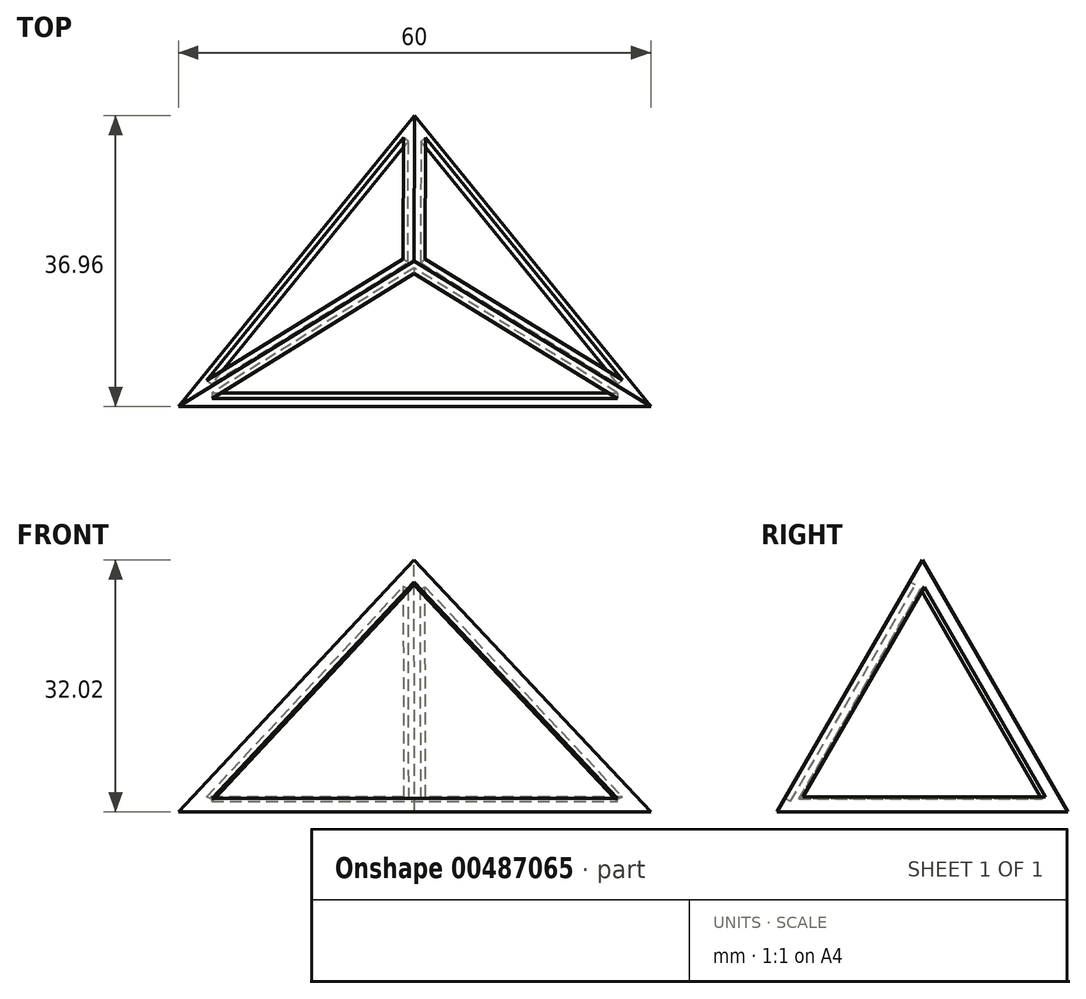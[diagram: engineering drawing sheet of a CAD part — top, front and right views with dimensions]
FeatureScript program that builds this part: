
annotation { "Feature Type Name" : "Feature", "Feature Type Description" : "" }
export const myFeature = defineFeature(function(context is Context, id is Id, definition is map)
    precondition{}
    {
        {
            var Q0;
            Q0=qCreatedBy(makeId("Top.planeOp"),FACE);
            var sketch = newSketch(context, id + "F0", { "sketchPlane" : qUnion([Q0])});
            skLineSegment(sketch, "E0.bottom", {"start": v(30, -36.96) * mm, "end": v(-30, -36.96) * mm});
            skPoint(sketch, "E0.middle", {"position": v(0, 0) * mm});
            skLineSegment(sketch, "E1", {"start": v(30, -36.96) * mm, "end": v(0, 0) * mm});
            skLineSegment(sketch, "E2", {"start": v(-30, -36.96) * mm, "end": v(0, 0) * mm});
            skSolve(sketch);
        }
        {
            var Q0;
            Q0=sQuery(id+"F0.wireOp",EDGE,"E0.bottom");
            cPlane(context, id + "F1", {"entities" : qUnion([Q0]), "cplaneType" : CPlaneType.LINE_ANGLE, "offset" : 25.4 * mm, "angle" : 30 * degree, "width" : 152.4 * mm, "height" : 152.4 * mm});
        }
        {
            var Q0;
            Q0=qCreatedBy(id+"F1.planeOp",FACE);
            var sketch = newSketch(context, id + "F2", { "sketchPlane" : qUnion([Q0])});
            skLineSegment(sketch, "E3.bottom", {"start": v(29.92, -18.46) * mm, "end": v(-30.08, -18.46) * mm});
            skLineSegment(sketch, "E4", {"start": v(29.92, -18.46) * mm, "end": v(-0.08, 18.5) * mm});
            skLineSegment(sketch, "E5", {"start": v(-30.08, -18.46) * mm, "end": v(-0.08, 18.5) * mm});
            skSolve(sketch);
        }
        {
            var Q0;
            Q0=makeQuery(id+"F0.imprint","IMPRINT",FACE,{"disambiguationData":[TD([[makeQuery(id+"F0.imprint","IMPRINT",EDGE,{"derivedFrom":sQuery(id+"F0.wireOp",EDGE,"E0.bottom")}),-1.0]])]});
            var Q1;
            Q1=sQuery(id+"F2.wireOp",VERTEX,"E5.end");
            loft(context, id + "F3", {"sheetProfilesArray" : [{ "sheetProfileEntities" : qUnion([Q0]) }, { "sheetProfileEntities" : qUnion([Q1]) }]});
        }
        {
            var Q0;
            {var subQ0=sQuery(id+"F0.wireOp",EDGE,"E2");var subQ1=sQuery(id+"F0.wireOp",EDGE,"E1");var subQ2=sQuery(id+"F0.wireOp",EDGE,"E0.bottom");Q0=makeQuery(id+"F3.opLoft","SWEPT_FACE",FACE,{"disambiguationData":[OSD([subQ2,subQ1,subQ0]),TDD([makeQuery(id+"F0.imprint","INTERSECT",VERTEX,{"derivedFrom":[subQ2,subQ0]}),makeQuery(id+"F0.imprint","INTERSECT",VERTEX,{"derivedFrom":[subQ1,subQ0]}),makeQuery(id+"F0.imprint","IMPRINT",EDGE,{"derivedFrom":subQ0})])]});}
            var sketch = newSketch(context, id + "F4", { "sketchPlane" : qUnion([Q0])});
            skLineSegment(sketch, "E6.0", {"start": v(41.78, -9.43) * mm, "end": v(22.63, 25.33) * mm});
            skLineSegment(sketch, "E6.1", {"start": v(3.5, 1.14) * mm, "end": v(41.78, -9.43) * mm});
            skLineSegment(sketch, "E6.2", {"start": v(22.63, 25.33) * mm, "end": v(3.5, 1.14) * mm});
            skSolve(sketch);
        }
        {
            var Q0;
            {var subQ0=sQuery(id+"F0.wireOp",EDGE,"E0.bottom");var subQ1=sQuery(id+"F0.wireOp",EDGE,"E2");var subQ2=sQuery(id+"F0.wireOp",EDGE,"E1");Q0=makeQuery(id+"F3.opLoft","SWEPT_FACE",FACE,{"disambiguationData":[OSD([subQ0,subQ2,subQ1]),TDD([makeQuery(id+"F0.imprint","INTERSECT",VERTEX,{"derivedFrom":[subQ0,subQ2]}),makeQuery(id+"F0.imprint","INTERSECT",VERTEX,{"derivedFrom":[subQ0,subQ1]}),makeQuery(id+"F0.imprint","IMPRINT",EDGE,{"derivedFrom":subQ0})])]});}
            var sketch = newSketch(context, id + "F5", { "sketchPlane" : qUnion([Q0])});
            skLineSegment(sketch, "E7.0", {"start": v(25.75, -16.46) * mm, "end": v(-0.07, 15.28) * mm});
            skLineSegment(sketch, "E7.1", {"start": v(-25.76, -16.46) * mm, "end": v(25.75, -16.46) * mm});
            skLineSegment(sketch, "E7.2", {"start": v(-0.07, 15.28) * mm, "end": v(-25.76, -16.46) * mm});
            skSolve(sketch);
        }
        {
            var Q0;
            {var subQ0=sQuery(id+"F0.wireOp",EDGE,"E1");var subQ1=sQuery(id+"F0.wireOp",EDGE,"E2");var subQ2=sQuery(id+"F0.wireOp",EDGE,"E0.bottom");Q0=makeQuery(id+"F3.opLoft","SWEPT_FACE",FACE,{"disambiguationData":[OSD([subQ2,subQ0,subQ1]),TDD([makeQuery(id+"F0.imprint","INTERSECT",VERTEX,{"derivedFrom":[subQ2,subQ0]}),makeQuery(id+"F0.imprint","INTERSECT",VERTEX,{"derivedFrom":[subQ0,subQ1]}),makeQuery(id+"F0.imprint","IMPRINT",EDGE,{"derivedFrom":subQ0})])]});}
            var sketch = newSketch(context, id + "F6", { "sketchPlane" : qUnion([Q0])});
            skLineSegment(sketch, "E8.0", {"start": v(-3.51, 1.14) * mm, "end": v(-22.6, 25.31) * mm});
            skLineSegment(sketch, "E8.1", {"start": v(-41.72, -9.5) * mm, "end": v(-3.51, 1.14) * mm});
            skLineSegment(sketch, "E8.2", {"start": v(-22.6, 25.31) * mm, "end": v(-41.72, -9.5) * mm});
            skSolve(sketch);
        }
        {
            var Q0;
            Q0=makeQuery(id+"F5.imprint","IMPRINT",FACE,{"disambiguationData":[TD([[makeQuery(id+"F5.imprint","IMPRINT",EDGE,{"derivedFrom":sQuery(id+"F5.wireOp",EDGE,"E7.0")}),1.0]])]});
            extrude(context, id + "F7", {"entities" : qUnion([Q0]), "operationType" : NewBodyOperationType.REMOVE, "oppositeDirection" : true, "depth" : 0.81 * mm});
        }
        {
            var Q0;
            Q0=makeQuery(id+"F6.imprint","IMPRINT",FACE,{"disambiguationData":[TD([[makeQuery(id+"F6.imprint","IMPRINT",EDGE,{"derivedFrom":sQuery(id+"F6.wireOp",EDGE,"E8.0")}),1.0]])]});
            extrude(context, id + "F8", {"entities" : qUnion([Q0]), "operationType" : NewBodyOperationType.REMOVE, "oppositeDirection" : true, "depth" : 0.81 * mm});
        }
        {
            var Q0;
            Q0=makeQuery(id+"F4.imprint","IMPRINT",FACE,{"disambiguationData":[TD([[makeQuery(id+"F4.imprint","IMPRINT",EDGE,{"derivedFrom":sQuery(id+"F4.wireOp",EDGE,"E6.0")}),1.0]])]});
            extrude(context, id + "F9", {"entities" : qUnion([Q0]), "operationType" : NewBodyOperationType.REMOVE, "oppositeDirection" : true, "depth" : 0.81 * mm});
        }
    });
